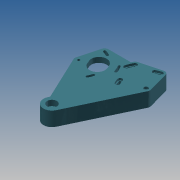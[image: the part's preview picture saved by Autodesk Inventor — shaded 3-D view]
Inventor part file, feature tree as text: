
AUTODESK INVENTOR PART (.ipt)
format: ipt  version: 2013 (Build 170138000, 138)  size: 386,560 bytes
history: native  units: mm
features: extrude x12, sketch x11, fillet x2, mirror x1, projected_geometry x1
ambient origin geometry x8: Origin, YZ Plane, XZ Plane, XY Plane, X Axis, Y Axis, Z Axis, Center Point
bodies: Solid1 (feature_tree)
feature tree (27):
  extrude  "Extrusion1"  Depth=42.0mm
  fillet  "Fillet1"  Radius=31.0mm
  extrude  "Extrusion2"  Depth=5.5mm
  extrude  "Extrusion3"  Depth=3.5mm
  mirror  "Mirror1"
  sketch  "Sketch4"  dims[d8=5.5mm d9=5.5mm]
  extrude  "Extrusion4"  Depth=5.5mm
  extrude  "Extrusion5"  Depth=5.5mm
  extrude  "Extrusion6"  Depth=5.0mm TaperAngle=0.0deg
  extrude  "Extrusion7"  Depth=5.0mm TaperAngle=0.0deg
  extrude  "Extrusion8"  Depth=8.5mm
  extrude  "Extrusion9"  Depth=22.5mm
  extrude  "Extrusion10"  Depth=20.0mm TaperAngle=0.0deg
  extrude  "Extrusion11"  Depth=3.0mm TaperAngle=0.0deg
  fillet  "Fillet4"  Radius=14.0mm
  extrude  "Extrusion12"  Depth=8.0mm TaperAngle=0.0deg
  sketch  "Sketch1"  dims[d0=198.0mm d2=42.0mm d3=31.0mm]
  sketch  "Sketch2"  dims[d4=5.5mm d5=5.5mm]
  sketch  "Sketch3"  dims[d6=5.0mm d7=3.5mm]
  projected_geometry  "Projected Loop1"
  sketch  "Sketch5"  dims[d10=5.0mm d11=0.0mm d12=5.5mm]
  sketch  "Sketch6"  dims[d13=5.0mm d14=0.0mm d15=5.0mm d16=0.0mm]
  sketch  "Sketch7"  dims[d17=25.0mm d19=5.0mm d20=0.0mm]
  sketch  "Sketch8"  dims[d21=16.0mm d22=0.0mm d23=8.5mm]
  sketch  "Sketch9"  dims[d26=20.0mm d27=0.0mm d28=22.5mm]
  sketch  "Sketch20"  dims[d30=20.0mm d31=0.0mm d32=20.0mm d33=0.0mm]
  sketch  "Sketch21"  dims[d34=6.0mm d36=3.0mm d37=0.0mm d38=14.0mm d40=8.0mm d41=0.0mm d57=25.0mm d58=5.5mm d59=10.0mm d60=0.0mm d61=5.5mm d62=2.5mm d63=0.0mm]
